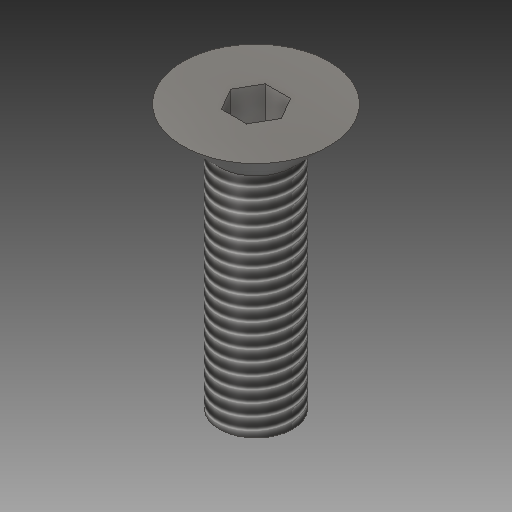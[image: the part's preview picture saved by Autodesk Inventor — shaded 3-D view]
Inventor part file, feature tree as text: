
AUTODESK INVENTOR PART (.ipt)
format: ipt  version: 2019 (Build 230136000, 136)  size: 161,280 bytes
history: native  units: mm
features: other x4, extrude x1
ambient origin geometry x8: Origin, YZ Plane, XZ Plane, XY Plane, X Axis, Y Axis, Z Axis, Center Point
bodies: Solid1 (feature_tree), Body (feature_tree)
feature tree (5):
  other  "Head"
  extrude  "Key Socket Cutout"  TaperAngle=0.0deg  [1 undecoded]
  other  "Head Revolution Profile"
  other  "Body Cross Section"
  other  "Key Socket Cutout Outline"
note: 1 required parameter value undecoded (feature->parameter linkage not recoverable at this tier; creation-order binding heuristic only, values carry confidence <= 0.55)
